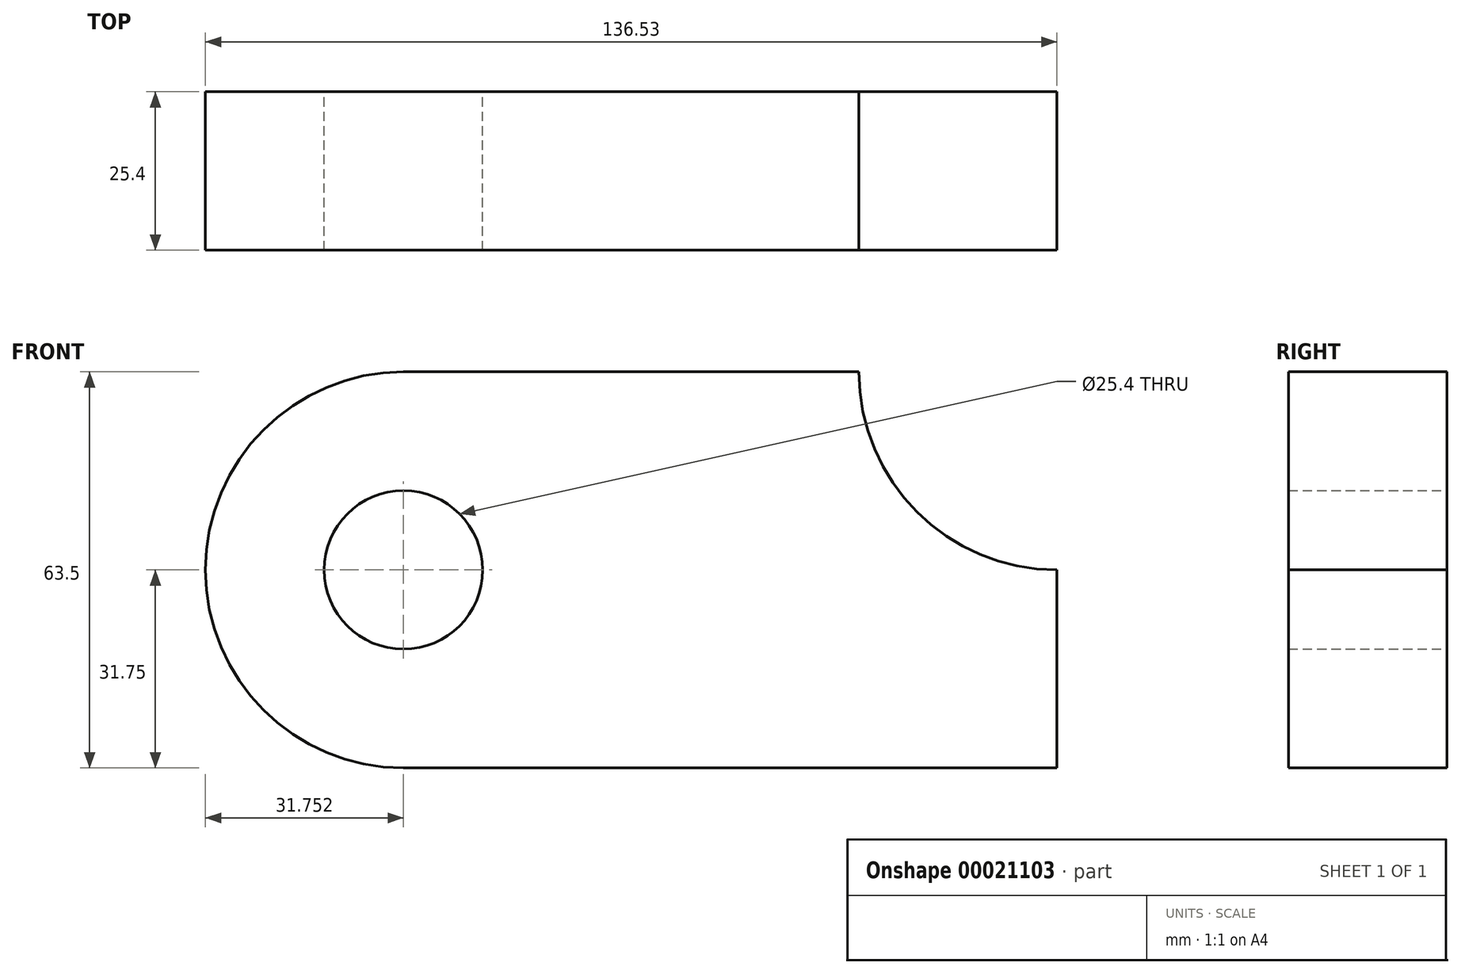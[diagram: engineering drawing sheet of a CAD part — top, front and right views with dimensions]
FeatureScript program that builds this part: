
annotation { "Feature Type Name" : "Feature", "Feature Type Description" : "" }
export const myFeature = defineFeature(function(context is Context, id is Id, definition is map)
    precondition{}
    {
        {
            var Q0;
            Q0=qCreatedBy(makeId("Front.planeOp"),FACE);
            var sketch = newSketch(context, id + "F0", { "sketchPlane" : qUnion([Q0])});
            skLineSegment(sketch, "E0.rect.bottom", {"start": v(-52.39, 31.75) * mm, "end": v(52.39, 31.75) * mm});
            skLineSegment(sketch, "E0.rect.top", {"start": v(-52.39, -31.75) * mm, "end": v(52.39, -31.75) * mm});
            skLineSegment(sketch, "E0.rect.left", {"start": v(-52.39, 31.75) * mm, "end": v(-52.39, -31.75) * mm});
            skLineSegment(sketch, "E0.rect.right", {"start": v(52.39, 31.75) * mm, "end": v(52.39, -31.75) * mm});
            skPoint(sketch, "E0.rect.middle", {"position": v(0, 0) * mm});
            skCircle(sketch, "E1", {"center": v(-52.39, 0) * mm, "radius": 31.75 * mm});
            skCircle(sketch, "E2", {"center": v(-52.39, 0) * mm, "radius": 12.7 * mm});
            skCircle(sketch, "E3", {"center": v(52.39, 31.75) * mm, "radius": 31.75 * mm});
            skSolve(sketch);
        }
        {
            var Q0;
            {var subQ0=sQuery(id+"F0.wireOp",EDGE,"E2");var subQ1=sQuery(id+"F0.wireOp",EDGE,"E0.rect.left");var subQ3=makeQuery(id+"F0.imprint","INTERSECT",VERTEX,{"disambiguationData":[OD(0.0)],"derivedFrom":[subQ1,subQ0]});Q0=makeQuery(id+"F0.imprint","IMPRINT",FACE,{"disambiguationData":[TD([[makeQuery(id+"F0.imprint","IMPRINT",EDGE,{"disambiguationData":[TD([[subQ3,1.0]])],"derivedFrom":subQ0}),-1.0]])]});}
            var Q1;
            {var subQ0=sQuery(id+"F0.wireOp",EDGE,"E2");var subQ1=sQuery(id+"F0.wireOp",EDGE,"E0.rect.left");var subQ3=makeQuery(id+"F0.imprint","INTERSECT",VERTEX,{"disambiguationData":[OD(0.0)],"derivedFrom":[subQ1,subQ0]});Q1=makeQuery(id+"F0.imprint","IMPRINT",FACE,{"disambiguationData":[TD([[makeQuery(id+"F0.imprint","IMPRINT",EDGE,{"disambiguationData":[TD([[subQ3,-1.0]])],"derivedFrom":subQ0}),-1.0]])]});}
            var Q2;
            {var subQ6=sQuery(id+"F0.wireOp",EDGE,"E0.rect.top");Q2=makeQuery(id+"F0.imprint","IMPRINT",FACE,{"disambiguationData":[TD([[makeQuery(id+"F0.imprint","IMPRINT",EDGE,{"derivedFrom":subQ6}),1.0]])]});}
            extrude(context, id + "F1", {"entities" : qUnion([Q0, Q1, Q2]), "depth" : 25.4 * mm});
        }
    });
